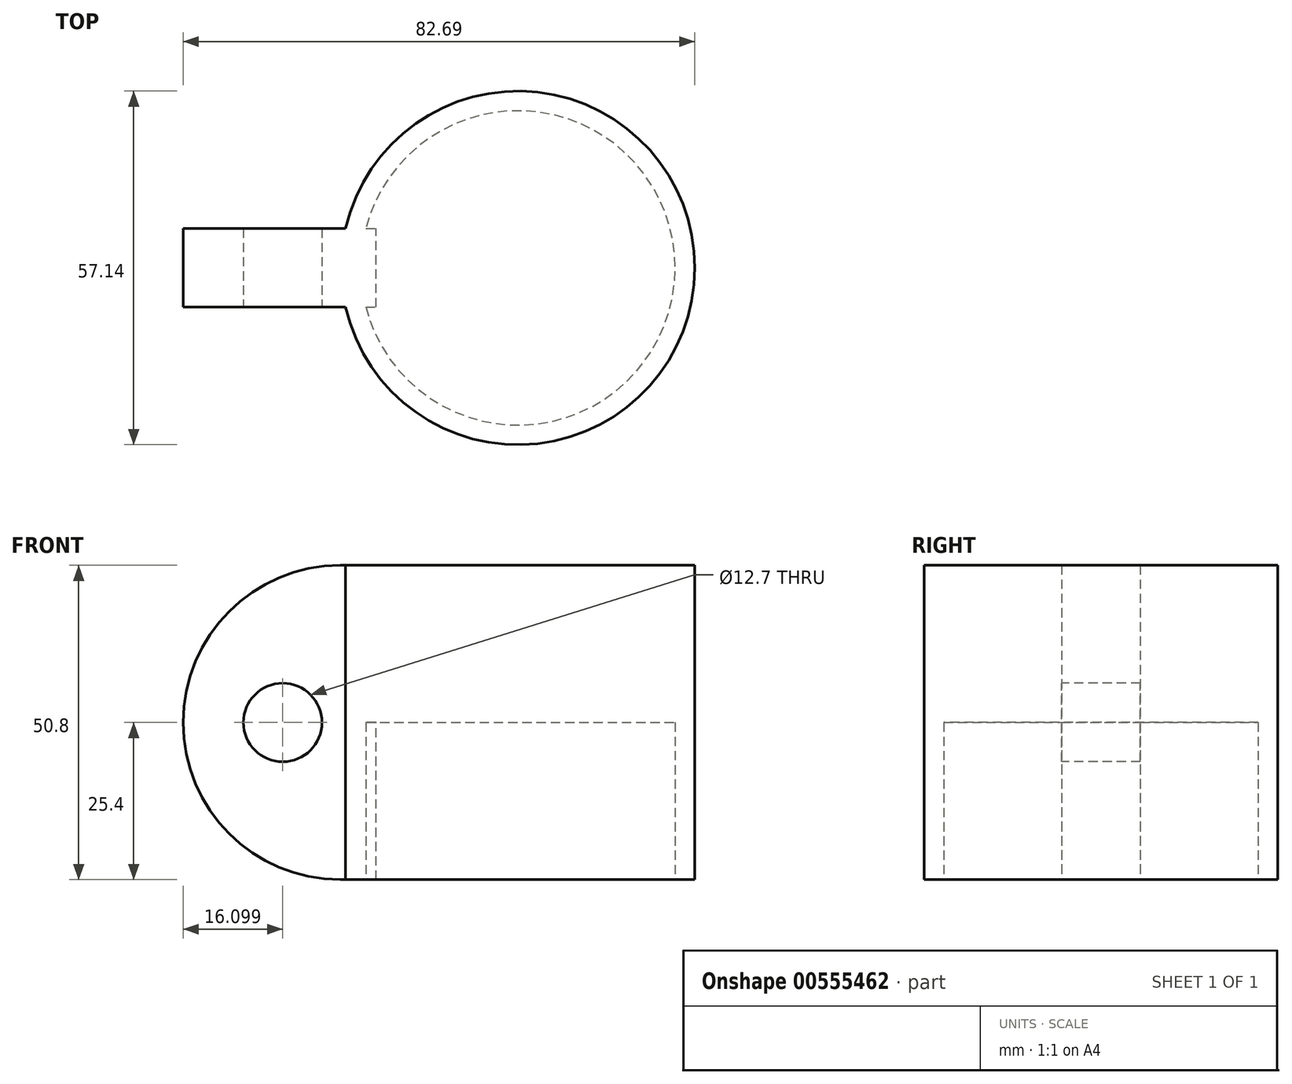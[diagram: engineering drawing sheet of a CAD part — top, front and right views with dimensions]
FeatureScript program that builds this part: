
annotation { "Feature Type Name" : "Feature", "Feature Type Description" : "" }
export const myFeature = defineFeature(function(context is Context, id is Id, definition is map)
    precondition{}
    {
        {
            var Q0;
            Q0=qCreatedBy(makeId("Top.planeOp"),FACE);
            var sketch = newSketch(context, id + "F0", { "sketchPlane" : qUnion([Q0])});
            skCircle(sketch, "E0", {"center": v(0, 0) * mm, "radius": 28.58 * mm});
            skSolve(sketch);
        }
        {
            var Q0;
            Q0=makeQuery(id+"F0.imprint","IMPRINT",FACE,{"disambiguationData":[TD([[makeQuery(id+"F0.imprint","IMPRINT",EDGE,{"derivedFrom":sQuery(id+"F0.wireOp",EDGE,"E0")}),1.0]])]});
            extrude(context, id + "F1", {"entities" : qUnion([Q0]), "depth" : 50.8 * mm, "offsetDistance" : 25.4 * mm});
        }
        {
            var Q0;
            Q0=makeQuery(id+"F1.opExtrude","CAP_FACE",FACE,{"disambiguationData":[OSD([sQuery(id+"F0.wireOp",EDGE,"E0")])],"isStart":true});
            var sketch = newSketch(context, id + "F2", { "sketchPlane" : qUnion([Q0])});
            skCircle(sketch, "E1", {"center": v(0, 0) * mm, "radius": 25.4 * mm});
            skSolve(sketch);
        }
        {
            var Q0;
            Q0=makeQuery(id+"F2.imprint","IMPRINT",FACE,{"disambiguationData":[TD([[makeQuery(id+"F2.imprint","IMPRINT",EDGE,{"derivedFrom":sQuery(id+"F2.wireOp",EDGE,"E1")}),1.0]])]});
            extrude(context, id + "F3", {"entities" : qUnion([Q0]), "operationType" : NewBodyOperationType.REMOVE, "oppositeDirection" : true, "depth" : 25.4 * mm, "offsetDistance" : 25.4 * mm});
        }
        {
            var Q0;
            Q0=qCreatedBy(makeId("Front.planeOp"),FACE);
            var sketch = newSketch(context, id + "F4", { "sketchPlane" : qUnion([Q0])});
            skLineSegment(sketch, "E2.bottom", {"start": v(-28.72, 0) * mm, "end": v(-22.92, 0) * mm});
            skLineSegment(sketch, "E2.top", {"start": v(-28.72, 50.8) * mm, "end": v(-22.92, 50.8) * mm});
            skLineSegment(sketch, "E2.right", {"start": v(-22.92, 0) * mm, "end": v(-22.92, 50.8) * mm});
            skArc(sketch, "E3", {"start": v(-28.72, 50.8) * mm, "mid": v(-54.12, 25.4) * mm, "end": v(-28.72, 0) * mm});
            skSolve(sketch);
        }
        {
            var Q0;
            Q0=makeQuery(id+"F4.imprint","IMPRINT",FACE,{"disambiguationData":[TD([[makeQuery(id+"F4.imprint","IMPRINT",EDGE,{"derivedFrom":sQuery(id+"F4.wireOp",EDGE,"E2.bottom")}),1.0]])]});
            extrude(context, id + "F5", {"entities" : qUnion([Q0]), "operationType" : NewBodyOperationType.ADD, "depth" : 6.35 * mm, "offsetDistance" : 25.4 * mm, "hasSecondDirection" : true, "secondDirectionOppositeDirection" : true, "secondDirectionDepth" : 6.35 * mm});
        }
        {
            var Q0;
            {var subQ0=sQuery(id+"F4.wireOp",EDGE,"E2.bottom");var subQ1=sQuery(id+"F0.wireOp",EDGE,"E0");var subQ2=sQuery(id+"F4.wireOp",EDGE,"E3");var subQ3=sQuery(id+"F4.wireOp",EDGE,"E2.top");Q0=makeQuery(id+"F5.boolean.opBoolean","SPLIT",FACE,{"disambiguationData":[TD([makeQuery(id+"F1.opExtrude","SWEPT_FACE",FACE,{"disambiguationData":[OSD([subQ1])]})])],"derivedFrom":makeQuery(id+"F5.opExtrude","CAP_FACE",FACE,{"disambiguationData":[OSD([subQ0,subQ3,sQuery(id+"F4.wireOp",EDGE,"E2.right"),subQ2])],"isStart":false})});}
            var sketch = newSketch(context, id + "F6", { "sketchPlane" : qUnion([Q0])});
            skCircle(sketch, "E4", {"center": v(-38.02, 25.4) * mm, "radius": 6.35 * mm});
            skSolve(sketch);
        }
        {
            var Q0;
            Q0=qSketchRegion(id+"F6",true);
            extrude(context, id + "F7", {"entities" : qUnion([Q0]), "operationType" : NewBodyOperationType.REMOVE, "oppositeDirection" : true, "depth" : 25.4 * mm, "offsetDistance" : 25.4 * mm});
        }
        {
            var Q0;
            Q0=qCreatedBy(makeId("Front.planeOp"),FACE);
            var sketch = newSketch(context, id + "F8", { "sketchPlane" : qUnion([Q0])});
            skLineSegment(sketch, "E5", {"start": v(0, -12.95) * mm, "end": v(0, 52.58) * mm});
            skSolve(sketch);
        }
    });
